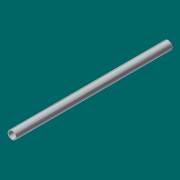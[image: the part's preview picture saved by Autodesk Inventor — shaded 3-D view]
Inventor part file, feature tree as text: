
AUTODESK INVENTOR PART (.ipt)
format: ipt  version: 2017 (Build 210142000, 142)  size: 74,240 bytes
history: native  units: in
note: dims shown in document units (in); Inventor stores cm internally (conversion verified against a paired STEP export)
features: extrude x1, sketch x1
ambient origin geometry x8: Origin, YZ Plane, XZ Plane, XY Plane, X Axis, Y Axis, Z Axis, Center Point
bodies: Solid1 (feature_tree)
feature tree (2):
  extrude  "Extrusion1"  Depth=54.25in
  sketch  "Sketch1"  dims[d0=2.875in d1=2.469in d2=54.25in d3=0.0in]
